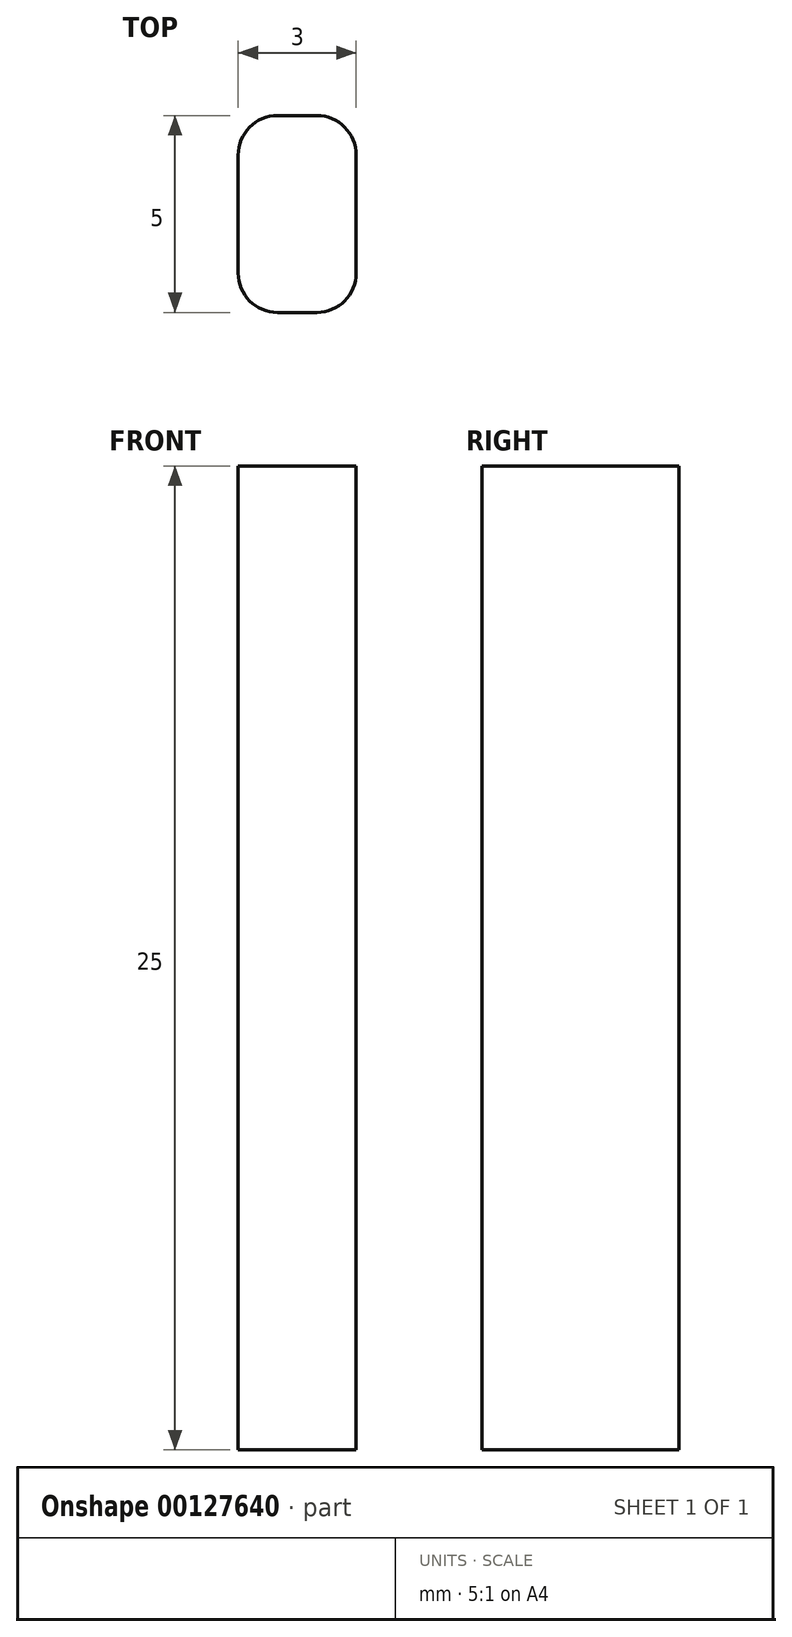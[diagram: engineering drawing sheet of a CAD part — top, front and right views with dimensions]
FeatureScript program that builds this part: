
annotation { "Feature Type Name" : "Feature", "Feature Type Description" : "" }
export const myFeature = defineFeature(function(context is Context, id is Id, definition is map)
    precondition{}
    {
        {
            var Q0;
            Q0=qCreatedBy(makeId("Top.planeOp"),FACE);
            var sketch = newSketch(context, id + "F0", { "sketchPlane" : qUnion([Q0])});
            skLineSegment(sketch, "E0.bottom", {"start": v(0, 0) * mm, "end": v(3, 0) * mm});
            skLineSegment(sketch, "E0.top", {"start": v(0, -5) * mm, "end": v(3, -5) * mm});
            skLineSegment(sketch, "E0.left", {"start": v(0, 0) * mm, "end": v(0, -5) * mm});
            skLineSegment(sketch, "E0.right", {"start": v(3, 0) * mm, "end": v(3, -5) * mm});
            skSolve(sketch);
        }
        {
            var Q0;
            Q0 = qSketchRegion(id + "F0", true);
            var Q1;
            Q1=makeQuery(id+"F0.imprint","IMPRINT",FACE,{"disambiguationData":[TD([[makeQuery(id+"F0.imprint","IMPRINT",EDGE,{"derivedFrom":sQuery(id+"F0.wireOp",EDGE,"E0.bottom")}),-1.0]])]});
            extrude(context, id + "F1", {"entities" : qUnion([Q0, Q1]), "depth" : 25 * mm});
        }
        {
            var Q0;
            Q0=makeQuery(id+"F1.opExtrude","SWEPT_EDGE",EDGE,{"disambiguationData":[OSD([sQuery(id+"F0.wireOp",EDGE,"E0.bottom"),sQuery(id+"F0.wireOp",EDGE,"E0.left")])]});
            var Q1;
            Q1=makeQuery(id+"F1.opExtrude","SWEPT_EDGE",EDGE,{"disambiguationData":[OSD([sQuery(id+"F0.wireOp",EDGE,"E0.top"),sQuery(id+"F0.wireOp",EDGE,"E0.left")])]});
            var Q2;
            Q2=makeQuery(id+"F1.opExtrude","SWEPT_EDGE",EDGE,{"disambiguationData":[OSD([sQuery(id+"F0.wireOp",EDGE,"E0.top"),sQuery(id+"F0.wireOp",EDGE,"E0.right")])]});
            var Q3;
            Q3=makeQuery(id+"F1.opExtrude","SWEPT_EDGE",EDGE,{"disambiguationData":[OSD([sQuery(id+"F0.wireOp",EDGE,"E0.bottom"),sQuery(id+"F0.wireOp",EDGE,"E0.right")])]});
            fillet(context, id + "F2", {"entities" : qUnion([Q0, Q1, Q2, Q3]), "radius" : 1 * mm, "tangentPropagation" : true, "allowEdgeOverflow" : false});
        }
    });
